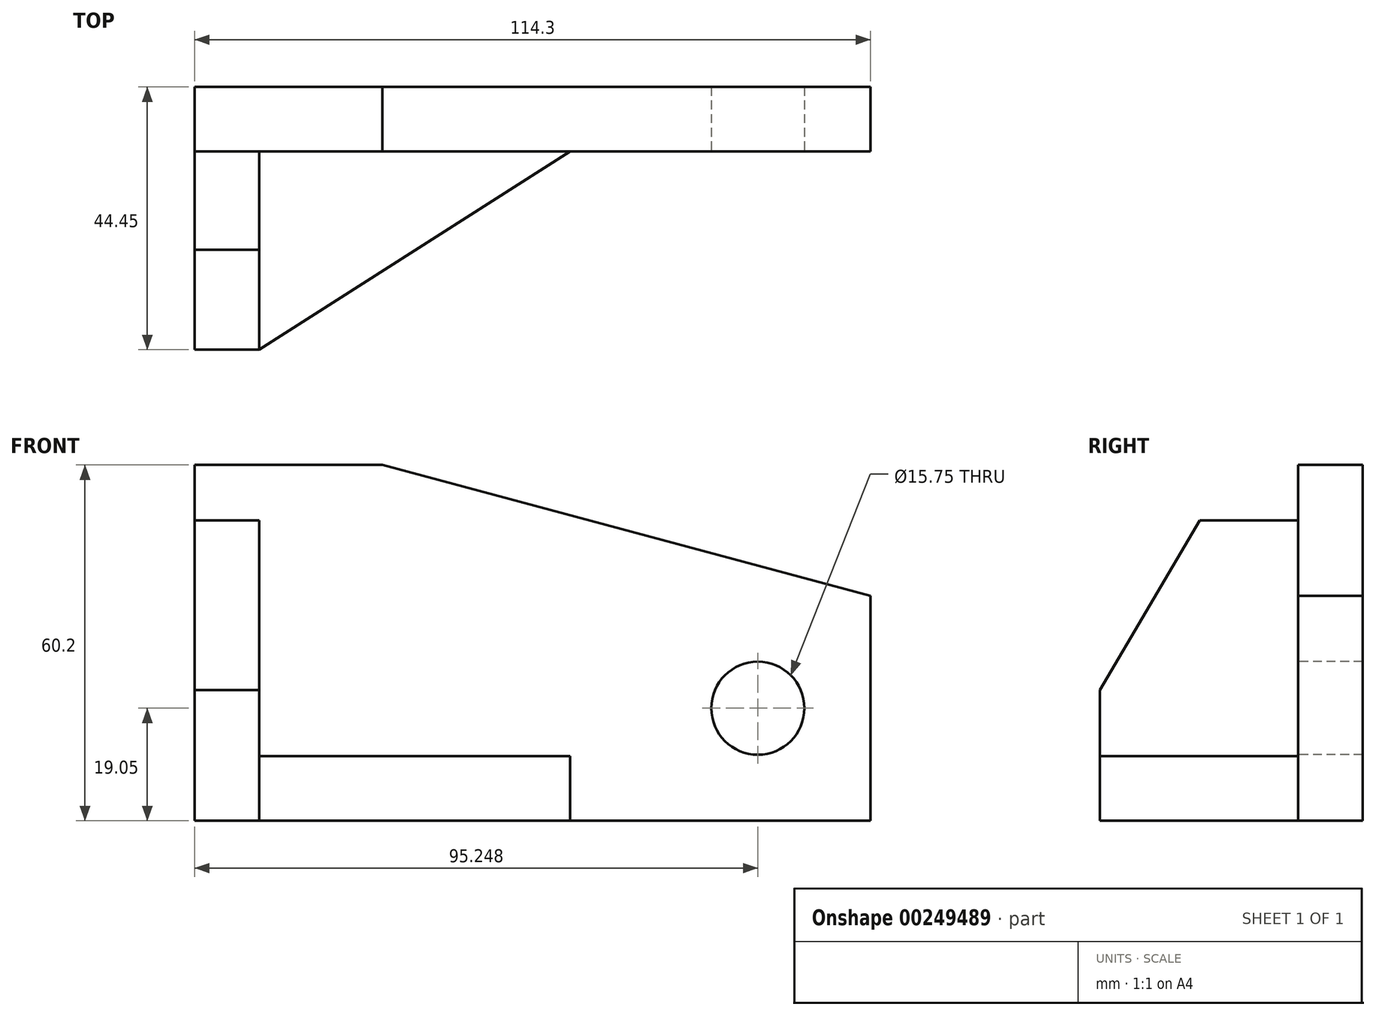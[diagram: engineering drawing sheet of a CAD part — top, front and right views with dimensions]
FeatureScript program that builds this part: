
annotation { "Feature Type Name" : "Feature", "Feature Type Description" : "" }
export const myFeature = defineFeature(function(context is Context, id is Id, definition is map)
    precondition{}
    {
        {
            var Q0;
            Q0=qCreatedBy(makeId("Right.planeOp"),FACE);
            var sketch = newSketch(context, id + "F0", { "sketchPlane" : qUnion([Q0])});
            skLineSegment(sketch, "E0.bottom", {"start": v(0, 0) * mm, "end": v(-33.53, 0) * mm});
            skLineSegment(sketch, "E0.top", {"start": v(0, 50.8) * mm, "end": v(-16.61, 50.8) * mm});
            skLineSegment(sketch, "E0.left", {"start": v(0, 0) * mm, "end": v(0, 50.8) * mm});
            skLineSegment(sketch, "E0.right", {"start": v(-33.53, 0) * mm, "end": v(-33.53, 22.1) * mm});
            skLineSegment(sketch, "E1", {"start": v(-16.61, 50.8) * mm, "end": v(-33.53, 22.1) * mm});
            skPoint(sketch, "E2.orphan", {"position": v(-33.53, 50.8) * mm});
            skPoint(sketch, "E3.top.end.orphan", {"position": v(-16.96, 22.1) * mm});
            skSolve(sketch);
        }
        {
            var Q0;
            Q0=qCreatedBy(makeId("Top.planeOp"),FACE);
            var sketch = newSketch(context, id + "F1", { "sketchPlane" : qUnion([Q0])});
            skLineSegment(sketch, "E4.left", {"start": v(0, 0) * mm, "end": v(0, -33.53) * mm});
            skLineSegment(sketch, "E5.bottom", {"start": v(0, 0) * mm, "end": v(52.58, 0) * mm});
            skLineSegment(sketch, "E6", {"start": v(52.58, 0) * mm, "end": v(0, -33.53) * mm});
            skSolve(sketch);
        }
        {
            var Q0;
            Q0=qCreatedBy(makeId("Front.planeOp"),FACE);
            var sketch = newSketch(context, id + "F2", { "sketchPlane" : qUnion([Q0])});
            skPoint(sketch, "E7.orphan", {"position": v(17.11, 0) * mm});
            skLineSegment(sketch, "E8.bottom", {"start": v(0, 0) * mm, "end": v(-10.92, 0) * mm});
            skLineSegment(sketch, "E8.top", {"start": v(0, 60.2) * mm, "end": v(-10.92, 60.2) * mm});
            skLineSegment(sketch, "E8.left", {"start": v(0, 0) * mm, "end": v(0, 60.2) * mm});
            skLineSegment(sketch, "E8.right", {"start": v(-10.92, 0) * mm, "end": v(-10.92, 60.2) * mm});
            skLineSegment(sketch, "E9.bottom", {"start": v(0, 0) * mm, "end": v(103.38, 0) * mm});
            skLineSegment(sketch, "E9.top", {"start": v(0, 60.2) * mm, "end": v(20.83, 60.2) * mm});
            skLineSegment(sketch, "E9.right", {"start": v(103.38, 0) * mm, "end": v(103.38, 38.08) * mm});
            skLineSegment(sketch, "E10.bottom", {"start": v(-10.92, 60.2) * mm, "end": v(20.83, 60.2) * mm});
            skLineSegment(sketch, "E11.bottom", {"start": v(103.38, 0) * mm, "end": v(84.33, 0) * mm});
            skLineSegment(sketch, "E11.left", {"start": v(103.38, 0) * mm, "end": v(103.38, 19.05) * mm});
            skCircle(sketch, "E12", {"center": v(84.33, 19.05) * mm, "radius": 7.87 * mm});
            skLineSegment(sketch, "E13", {"start": v(20.83, 60.2) * mm, "end": v(103.38, 38.08) * mm});
            skSolve(sketch);
        }
        {
            var Q0;
            Q0=makeQuery(id+"F1.imprint","IMPRINT",FACE,{"disambiguationData":[TD([[makeQuery(id+"F1.imprint","IMPRINT",EDGE,{"derivedFrom":sQuery(id+"F1.wireOp",EDGE,"E5.bottom")}),-1.0]])]});
            extrude(context, id + "F3", {"entities" : qUnion([Q0]), "depth" : 10.92 * mm});
        }
        {
            var Q0;
            Q0=makeQuery(id+"F2.imprint","IMPRINT",FACE,{"disambiguationData":[TD([[makeQuery(id+"F2.imprint","IMPRINT",EDGE,{"derivedFrom":sQuery(id+"F2.wireOp",EDGE,"E9.bottom")}),1.0]])]});
            var Q1;
            Q1=makeQuery(id+"F2.imprint","IMPRINT",FACE,{"disambiguationData":[TD([[makeQuery(id+"F2.imprint","IMPRINT",EDGE,{"derivedFrom":sQuery(id+"F2.wireOp",EDGE,"E8.bottom")}),-1.0]])]});
            extrude(context, id + "F4", {"entities" : qUnion([Q0, Q1]), "operationType" : NewBodyOperationType.ADD, "oppositeDirection" : true, "depth" : 10.92 * mm});
        }
        {
            var Q0;
            Q0=makeQuery(id+"F0.imprint","IMPRINT",FACE,{"disambiguationData":[TD([[makeQuery(id+"F0.imprint","IMPRINT",EDGE,{"derivedFrom":sQuery(id+"F0.wireOp",EDGE,"E0.bottom")}),-1.0]])]});
            extrude(context, id + "F5", {"entities" : qUnion([Q0]), "operationType" : NewBodyOperationType.ADD, "oppositeDirection" : true, "depth" : 10.92 * mm});
        }
    });
